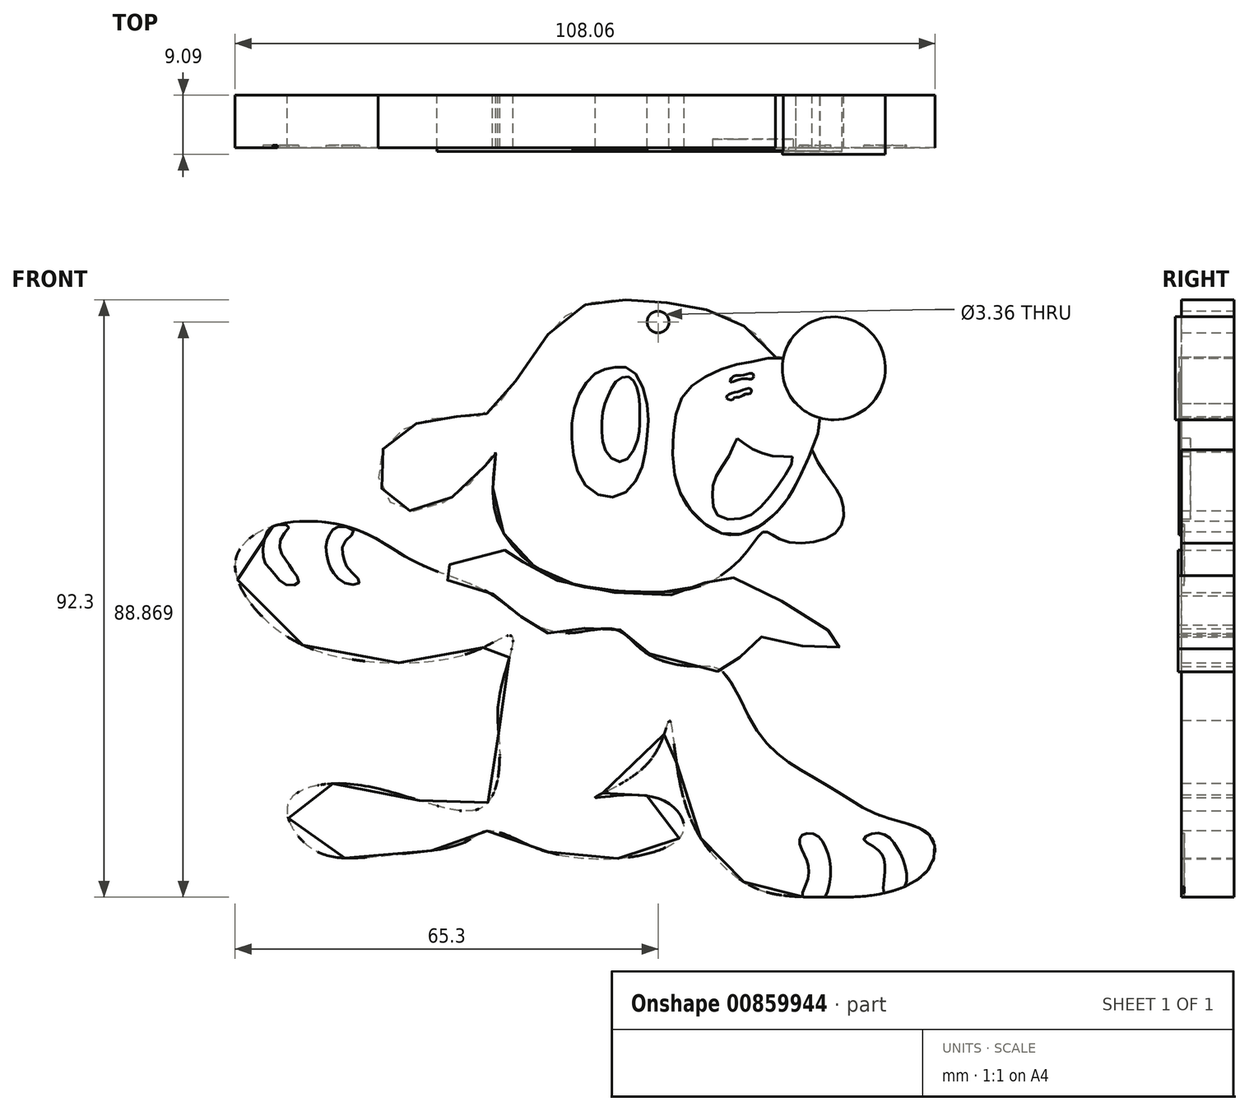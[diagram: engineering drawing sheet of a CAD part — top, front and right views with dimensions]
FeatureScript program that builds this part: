
annotation { "Feature Type Name" : "Feature", "Feature Type Description" : "" }
export const myFeature = defineFeature(function(context is Context, id is Id, definition is map)
    precondition{}
    {
        {
            var Q0;
            Q0=qCreatedBy(makeId("Front.planeOp"),FACE);
            var sketch = newSketch(context, id + "F0", { "sketchPlane" : qUnion([Q0])});
            skFitSpline(sketch, "E0", {"points": [v(-6.98, -2.09) * mm, v(5.98, -4.59) * mm, v(16.89, -3.45) * mm, v(23.93, 2.23) * mm, v(26.2, 4.73) * mm, v(28.93, 3.37) * mm, v(37.12, 4.5) * mm, v(38.03, 9.73) * mm, v(34.16, 15.87) * mm, v(27.8, 31.78) * mm, v(17.8, 38.83) * mm, v(6.66, 40.42) * mm, v(-4.7, 37.92) * mm, v(-16.07, 23.37) * mm, v(-22.66, 22.46) * mm, v(-32.9, 17.23) * mm, v(-30.4, 8.37) * mm, v(-18.8, 12.69) * mm, v(-15.39, 17) * mm, v(-15.62, 8.6) * mm, v(-6.98, -2.09) * mm]});
            skFitSpline(sketch, "E1", {"points": [v(-16.9, -4.46) * mm, v(-27.7, 0) * mm, v(-36.09, 4.73) * mm, v(-48.79, 5.81) * mm, v(-55.55, 0) * mm, v(-47.98, -11.22) * mm, v(-31.5, -15.54) * mm, v(-17.7, -13.38) * mm, v(-12.84, -11.49) * mm, v(-14.73, -20.4) * mm, v(-14.73, -29.33) * mm, v(-17.16, -37.7) * mm, v(-26.9, -36.9) * mm, v(-40.14, -34.2) * mm, v(-47.44, -37.44) * mm, v(-43.38, -44.47) * mm, v(-32.03, -45.28) * mm, v(-20.4, -43.38) * mm, v(-16.35, -41.5) * mm, v(-9.06, -44.2) * mm, v(0, -45.82) * mm, v(8.24, -45) * mm, v(13.65, -41.5) * mm, v(9.33, -36.36) * mm, v(0, -36.36) * mm, v(8.24, -30.95) * mm, v(11.49, -24.46) * mm, v(13.1, -34.2) * mm, v(17.16, -43.92) * mm, v(22.03, -48.79) * mm, v(27.44, -51.22) * mm, v(36.09, -51.76) * mm, v(44.2, -51.22) * mm, v(51.5, -47.44) * mm, v(51.76, -42.3) * mm, v(44.47, -39.33) * mm, v(37.98, -35.82) * mm, v(31.22, -31.76) * mm, v(25, -26.08) * mm, v(19.6, -16.9) * mm, v(15, -16.08) * mm, v(7.7, -13.92) * mm, v(3.1, -10.4) * mm, v(-4.73, -10.95) * mm, v(-12.03, -7.97) * mm, v(-16.9, -4.46) * mm]});
            skSolve(sketch);
        }
        {
            var Q0;
            Q0=makeQuery(id+"F0.imprint","IMPRINT",FACE,{"disambiguationData":[TD([[makeQuery(id+"F0.imprint","IMPRINT",EDGE,{"derivedFrom":sQuery(id+"F0.wireOp",EDGE,"E0")}),1.0]])]});
            var Q1;
            Q1=makeQuery(id+"F0.imprint","IMPRINT",FACE,{"disambiguationData":[TD([[makeQuery(id+"F0.imprint","IMPRINT",EDGE,{"derivedFrom":sQuery(id+"F0.wireOp",EDGE,"E1")}),1.0]])]});
            extrude(context, id + "F1", {"entities" : qUnion([Q0, Q1]), "depth" : 8.13 * mm, "offsetDistance" : 25.4 * mm});
        }
        {
            var Q0;
            Q0=qCreatedBy(makeId("Front.planeOp"),FACE);
            var sketch = newSketch(context, id + "F2", { "sketchPlane" : qUnion([Q0])});
            skFitSpline(sketch, "E2", {"points": [v(-11.05, 0) * mm, v(-12.34, 1.77) * mm, v(-24.36, -1.66) * mm, v(-16.85, -4.45) * mm, v(-10.84, -8.95) * mm, v(-5.7, -11.1) * mm, v(2.46, -9.81) * mm, v(8.68, -14.32) * mm, v(15.33, -15.82) * mm, v(20.91, -16.68) * mm, v(24.13, -11.96) * mm, v(32.28, -13.03) * mm, v(38.08, -12.82) * mm, v(32.5, -8.31) * mm, v(19.2, -2.09) * mm, v(15.33, -4.24) * mm, v(0, -4.24) * mm, v(-11.05, 0) * mm]});
            skSolve(sketch);
        }
        {
            var Q0;
            Q0=makeQuery(id+"F2.imprint","IMPRINT",FACE,{"disambiguationData":[TD([[makeQuery(id+"F2.imprint","IMPRINT",EDGE,{"derivedFrom":sQuery(id+"F2.wireOp",EDGE,"E2")}),1.0]])]});
            extrude(context, id + "F3", {"entities" : qUnion([Q0]), "depth" : 8.7 * mm, "offsetDistance" : 25.4 * mm});
        }
        {
            var Q0;
            Q0=qCreatedBy(makeId("Front.planeOp"),FACE);
            var sketch = newSketch(context, id + "F4", { "sketchPlane" : qUnion([Q0])});
            skFitSpline(sketch, "E3", {"points": [v(29.36, 31.27) * mm, v(25.4, 31.2) * mm, v(21.32, 30.4) * mm, v(16.75, 28.49) * mm, v(13.44, 25.4) * mm, v(12.07, 19.76) * mm, v(12.54, 12.37) * mm, v(15.72, 7) * mm, v(21.51, 4.18) * mm, v(28.02, 7.73) * mm, v(31.67, 13.37) * mm, v(34.78, 21.98) * mm, v(33.52, 23.16) * mm, v(29.9, 26.02) * mm, v(29.36, 31.27) * mm]});
            skSolve(sketch);
        }
        {
            var Q0;
            Q0=makeQuery(id+"F4.imprint","IMPRINT",FACE,{"disambiguationData":[TD([[makeQuery(id+"F4.imprint","IMPRINT",EDGE,{"derivedFrom":sQuery(id+"F4.wireOp",EDGE,"E3")}),1.0]])]});
            extrude(context, id + "F5", {"entities" : qUnion([Q0]), "operationType" : NewBodyOperationType.ADD, "depth" : 8.53 * mm, "offsetDistance" : 25.4 * mm});
        }
        {
            var Q0;
            Q0=qCreatedBy(makeId("Front.planeOp"),FACE);
            var sketch = newSketch(context, id + "F6", { "sketchPlane" : qUnion([Q0])});
            skCircle(sketch, "E4", {"center": v(36.86, 29.93) * mm, "radius": 7.96 * mm});
            skSolve(sketch);
        }
        {
            var Q0;
            Q0=makeQuery(id+"F6.imprint","IMPRINT",FACE,{"disambiguationData":[TD([[makeQuery(id+"F6.imprint","IMPRINT",EDGE,{"derivedFrom":sQuery(id+"F6.wireOp",EDGE,"E4")}),1.0]])]});
            extrude(context, id + "F7", {"entities" : qUnion([Q0]), "operationType" : NewBodyOperationType.ADD, "depth" : 9.1 * mm, "offsetDistance" : 25.4 * mm});
        }
        {
            var Q0;
            Q0=makeQuery(id+"F1.opExtrude","CAP_FACE",FACE,{"disambiguationData":[OSD([sQuery(id+"F0.wireOp",EDGE,"E1")])],"isStart":false});
            var sketch = newSketch(context, id + "F8", { "sketchPlane" : qUnion([Q0])});
            skFitSpline(sketch, "E5", {"points": [v(-49.78, 5.53) * mm, v(-50.84, 4.16) * mm, v(-51.23, 2.5) * mm, v(-51.01, 0) * mm, v(-49.74, -1.54) * mm, v(-47.9, -3.42) * mm, v(-45.78, -3.2) * mm, v(-46.46, -1.59) * mm, v(-47.52, 0) * mm, v(-48.5, 1.56) * mm, v(-48.42, 3.86) * mm, v(-47.27, 5.57) * mm, v(-49.78, 5.53) * mm]});
            skFitSpline(sketch, "E6", {"points": [v(-39.65, 5.44) * mm, v(-40.88, 4.42) * mm, v(-41.52, 2.63) * mm, v(-41.18, 0) * mm, v(-40.37, -1.67) * mm, v(-38.37, -3.33) * mm, v(-36.37, -3.08) * mm, v(-38.07, -1.07) * mm, v(-38.84, 0.76) * mm, v(-38.84, 2.84) * mm, v(-37.26, 4.76) * mm, v(-39.65, 5.44) * mm]});
            skFitSpline(sketch, "E7", {"points": [v(32.03, -51.7) * mm, v(32.77, -49.18) * mm, v(32.72, -46.2) * mm, v(31.7, -43.9) * mm, v(31.83, -42.28) * mm, v(33.96, -42.07) * mm, v(35.7, -44.37) * mm, v(36.38, -47.86) * mm, v(35.45, -51.76) * mm, v(34.21, -51.76) * mm, v(32.03, -51.7) * mm]});
            skFitSpline(sketch, "E8", {"points": [v(44.64, -51.18) * mm, v(44.68, -48.2) * mm, v(44.51, -45.65) * mm, v(43.15, -44.07) * mm, v(41.5, -42.8) * mm, v(42.94, -41.9) * mm, v(45.37, -42.5) * mm, v(46.86, -44.54) * mm, v(47.88, -47.05) * mm, v(47.77, -50.14) * mm, v(45.77, -50.84) * mm, v(44.64, -51.18) * mm]});
            skSolve(sketch);
        }
        {
            var Q0;
            Q0=makeQuery(id+"F8.imprint","IMPRINT",FACE,{"disambiguationData":[TD([[makeQuery(id+"F8.imprint","IMPRINT",EDGE,{"derivedFrom":sQuery(id+"F8.wireOp",EDGE,"E6")}),1.0]])]});
            var Q1;
            {var subQ0=sQuery(id+"F8.wireOp",EDGE,"E5");var subQ1=makeQuery(id+"F1.opExtrude","CAP_EDGE",EDGE,{"disambiguationData":[OSD([sQuery(id+"F0.wireOp",EDGE,"E1")])],"isStart":false});var subQ2=makeQuery(id+"F8.imprint","INTERSECT",VERTEX,{"disambiguationData":[OD(0.0)],"derivedFrom":[subQ1,subQ0]});Q1=makeQuery(id+"F8.imprint","IMPRINT",FACE,{"disambiguationData":[TD([[makeQuery(id+"F8.imprint","IMPRINT",EDGE,{"disambiguationData":[TD([[subQ2,-1.0]])],"derivedFrom":subQ0}),1.0]])]});}
            var Q2;
            {var subQ0=sQuery(id+"F8.wireOp",EDGE,"E8");var subQ1=makeQuery(id+"F1.opExtrude","CAP_EDGE",EDGE,{"disambiguationData":[OSD([sQuery(id+"F0.wireOp",EDGE,"E1")])],"isStart":false});var subQ2=makeQuery(id+"F8.imprint","INTERSECT",VERTEX,{"disambiguationData":[OD(0.0)],"derivedFrom":[subQ1,subQ0]});Q2=makeQuery(id+"F8.imprint","IMPRINT",FACE,{"disambiguationData":[TD([[makeQuery(id+"F8.imprint","IMPRINT",EDGE,{"disambiguationData":[TD([[subQ2,1.0]])],"derivedFrom":subQ0}),-1.0]])]});}
            var Q3;
            {var subQ0=sQuery(id+"F8.wireOp",EDGE,"E7");var subQ1=makeQuery(id+"F1.opExtrude","CAP_EDGE",EDGE,{"disambiguationData":[OSD([sQuery(id+"F0.wireOp",EDGE,"E1")])],"isStart":false});var subQ2=makeQuery(id+"F8.imprint","INTERSECT",VERTEX,{"disambiguationData":[OD(0.0)],"derivedFrom":[subQ1,subQ0]});Q3=makeQuery(id+"F8.imprint","IMPRINT",FACE,{"disambiguationData":[TD([[makeQuery(id+"F8.imprint","IMPRINT",EDGE,{"disambiguationData":[TD([[subQ2,1.0]])],"derivedFrom":subQ0}),-1.0]])]});}
            extrude(context, id + "F9", {"entities" : qUnion([Q0, Q1, Q2, Q3]), "operationType" : NewBodyOperationType.REMOVE, "oppositeDirection" : true, "depth" : 0.43 * mm, "offsetDistance" : 25.4 * mm});
        }
        {
            var Q0;
            Q0=qCreatedBy(makeId("Front.planeOp"),FACE);
            var sketch = newSketch(context, id + "F10", { "sketchPlane" : qUnion([Q0])});
            skFitSpline(sketch, "E9", {"points": [v(3.08, 30.1) * mm, v(0.64, 29.5) * mm, v(-1.79, 27.13) * mm, v(-3.41, 22.67) * mm, v(-3.41, 17.06) * mm, v(-1.18, 11.52) * mm, v(3.48, 10.17) * mm, v(6.8, 13.54) * mm, v(8.01, 19.09) * mm, v(8.01, 24.63) * mm, v(5.64, 29.7) * mm, v(3.08, 30.1) * mm]});
            skSolve(sketch);
        }
        {
            var Q0;
            Q0=makeQuery(id+"F10.imprint","IMPRINT",FACE,{"disambiguationData":[TD([[makeQuery(id+"F10.imprint","IMPRINT",EDGE,{"derivedFrom":sQuery(id+"F10.wireOp",EDGE,"E9")}),1.0]])]});
            extrude(context, id + "F11", {"entities" : qUnion([Q0]), "operationType" : NewBodyOperationType.ADD, "depth" : 8.25 * mm, "offsetDistance" : 25.4 * mm});
        }
        {
            var Q0;
            Q0=qCreatedBy(makeId("Front.planeOp"),FACE);
            var sketch = newSketch(context, id + "F12", { "sketchPlane" : qUnion([Q0])});
            skFitSpline(sketch, "E10", {"points": [v(5.18, 28.63) * mm, v(3.5, 28.13) * mm, v(2.16, 26.06) * mm, v(1.25, 23.49) * mm, v(1.03, 20.02) * mm, v(1.93, 16.68) * mm, v(4.37, 15.55) * mm, v(6.53, 18.8) * mm, v(6.9, 21.46) * mm, v(6.85, 24.7) * mm, v(6.26, 27.41) * mm, v(5.18, 28.63) * mm]});
            skSolve(sketch);
        }
        {
            var Q0;
            Q0=makeQuery(id+"F12.imprint","IMPRINT",FACE,{"disambiguationData":[TD([[makeQuery(id+"F12.imprint","IMPRINT",EDGE,{"derivedFrom":sQuery(id+"F12.wireOp",EDGE,"E10")}),1.0]])]});
            extrude(context, id + "F13", {"entities" : qUnion([Q0]), "operationType" : NewBodyOperationType.ADD, "depth" : 8.47 * mm, "offsetDistance" : 25.4 * mm});
        }
        {
            var Q0;
            Q0=makeQuery(id+"F5.opExtrude","CAP_FACE",FACE,{"disambiguationData":[OSD([sQuery(id+"F4.wireOp",EDGE,"E3")])],"isStart":false});
            var sketch = newSketch(context, id + "F14", { "sketchPlane" : qUnion([Q0])});
            skFitSpline(sketch, "E11", {"points": [v(21.92, 19.14) * mm, v(23.36, 18.05) * mm, v(25.78, 16.87) * mm, v(28.46, 16.27) * mm, v(30.47, 16.2) * mm, v(29.93, 14.39) * mm, v(27.82, 11.23) * mm, v(24.8, 7.85) * mm, v(21.99, 6.64) * mm, v(18.86, 7.27) * mm, v(18.2, 9.54) * mm, v(18.25, 12.12) * mm, v(19.37, 14.45) * mm, v(21.25, 17.67) * mm, v(21.92, 19.14) * mm]});
            skSolve(sketch);
        }
        {
            var Q0;
            Q0=makeQuery(id+"F14.imprint","IMPRINT",FACE,{"disambiguationData":[TD([[makeQuery(id+"F14.imprint","IMPRINT",EDGE,{"derivedFrom":sQuery(id+"F14.wireOp",EDGE,"E11")}),-1.0]])]});
            extrude(context, id + "F15", {"entities" : qUnion([Q0]), "operationType" : NewBodyOperationType.REMOVE, "oppositeDirection" : true, "depth" : 4.3 * mm, "offsetDistance" : 25.4 * mm});
        }
        {
            var Q0;
            Q0=makeQuery(id+"F15.boolean.opBoolean","COPY",FACE,{"derivedFrom":makeQuery(id+"F15.opExtrude","CAP_FACE",FACE,{"disambiguationData":[OSD([sQuery(id+"F14.wireOp",EDGE,"E11")])],"isStart":false})});
            extrude(context, id + "F16", {"entities" : qUnion([Q0]), "operationType" : NewBodyOperationType.ADD, "depth" : 2.5 * mm, "offsetDistance" : 25.4 * mm});
        }
        {
            var Q0;
            Q0=makeQuery(id+"F16.opExtrude","CAP_FACE",FACE,{"disambiguationData":[OSD([sQuery(id+"F14.wireOp",EDGE,"E11")])],"isStart":false});
            var sketch = newSketch(context, id + "F17", { "sketchPlane" : qUnion([Q0])});
            skFitSpline(sketch, "E12", {"points": [v(19.09, 13.52) * mm, v(20.54, 13.2) * mm, v(22.13, 12.3) * mm, v(24.03, 10.73) * mm, v(25.03, 8.69) * mm, v(24.98, 8) * mm, v(23.26, 6.94) * mm, v(21.36, 6.6) * mm, v(20.08, 6.7) * mm, v(18.86, 7.28) * mm, v(18.37, 8.13) * mm, v(18.2, 9.32) * mm, v(18.16, 11.42) * mm, v(18.43, 12.72) * mm, v(19.09, 13.52) * mm]});
            skSolve(sketch);
        }
        {
            var Q0;
            {var subQ0=sQuery(id+"F17.wireOp",EDGE,"E12");var subQ1=makeQuery(id+"F16.opExtrude","CAP_EDGE",EDGE,{"disambiguationData":[OSD([sQuery(id+"F14.wireOp",EDGE,"E11")])],"isStart":false});var subQ2=makeQuery(id+"F17.imprint","INTERSECT",VERTEX,{"disambiguationData":[OD(4.0)],"derivedFrom":[subQ1,subQ0]});var subQ9=makeQuery(id+"F17.imprint","INTERSECT",VERTEX,{"disambiguationData":[OD(2.0)],"derivedFrom":[subQ1,subQ0]});Q0=makeQuery(id+"F17.imprint","IMPRINT",FACE,{"disambiguationData":[TD([[makeQuery(id+"F17.imprint","IMPRINT",EDGE,{"disambiguationData":[TD([[subQ9,-1.0],[subQ2,1.0]])],"derivedFrom":subQ0}),-1.0]])]});}
            extrude(context, id + "F18", {"entities" : qUnion([Q0]), "operationType" : NewBodyOperationType.ADD, "depth" : 0.46 * mm, "offsetDistance" : 25.4 * mm});
        }
        {
            var Q0;
            Q0=qCreatedBy(makeId("Front.planeOp"),FACE);
            var sketch = newSketch(context, id + "F19", { "sketchPlane" : qUnion([Q0])});
            skCircle(sketch, "E13", {"center": v(9.72, 37.1) * mm, "radius": 1.68 * mm});
            skSolve(sketch);
        }
        {
            var Q0;
            Q0=makeQuery(id+"F19.imprint","IMPRINT",FACE,{"disambiguationData":[TD([[makeQuery(id+"F19.imprint","IMPRINT",EDGE,{"derivedFrom":sQuery(id+"F19.wireOp",EDGE,"E13")}),1.0]])]});
            extrude(context, id + "F20", {"entities" : qUnion([Q0]), "operationType" : NewBodyOperationType.REMOVE, "depth" : 10.06 * mm, "offsetDistance" : 25.4 * mm});
        }
        {
            var Q0;
            Q0=makeQuery(id+"F5.opExtrude","CAP_FACE",FACE,{"disambiguationData":[OSD([sQuery(id+"F4.wireOp",EDGE,"E3")])],"isStart":false});
            var sketch = newSketch(context, id + "F21", { "sketchPlane" : qUnion([Q0])});
            skFitSpline(sketch, "E14", {"points": [v(20.83, 27.84) * mm, v(21.96, 28.11) * mm, v(23.43, 28.33) * mm, v(24.31, 28.36) * mm, v(24.36, 29.1) * mm, v(22.8, 28.89) * mm, v(21.43, 28.72) * mm, v(20.83, 27.84) * mm]});
            skFitSpline(sketch, "E15", {"points": [v(20.25, 25.37) * mm, v(20.75, 25.96) * mm, v(21.93, 26.29) * mm, v(23.07, 26.7) * mm, v(24.04, 26.73) * mm, v(24, 26.07) * mm, v(23.1, 25.93) * mm, v(22.28, 25.47) * mm, v(21.54, 25.4) * mm, v(21.15, 25.06) * mm, v(20.25, 25.37) * mm]});
            skSolve(sketch);
        }
        {
            var Q0;
            Q0=makeQuery(id+"F21.imprint","IMPRINT",FACE,{"disambiguationData":[TD([[makeQuery(id+"F21.imprint","IMPRINT",EDGE,{"derivedFrom":sQuery(id+"F21.wireOp",EDGE,"E14")}),1.0]])]});
            var Q1;
            Q1=makeQuery(id+"F21.imprint","IMPRINT",FACE,{"disambiguationData":[TD([[makeQuery(id+"F21.imprint","IMPRINT",EDGE,{"derivedFrom":sQuery(id+"F21.wireOp",EDGE,"E15")}),-1.0]])]});
            extrude(context, id + "F22", {"entities" : qUnion([Q0, Q1]), "operationType" : NewBodyOperationType.ADD, "depth" : 0.08 * mm, "offsetDistance" : 25.4 * mm});
        }
    });
